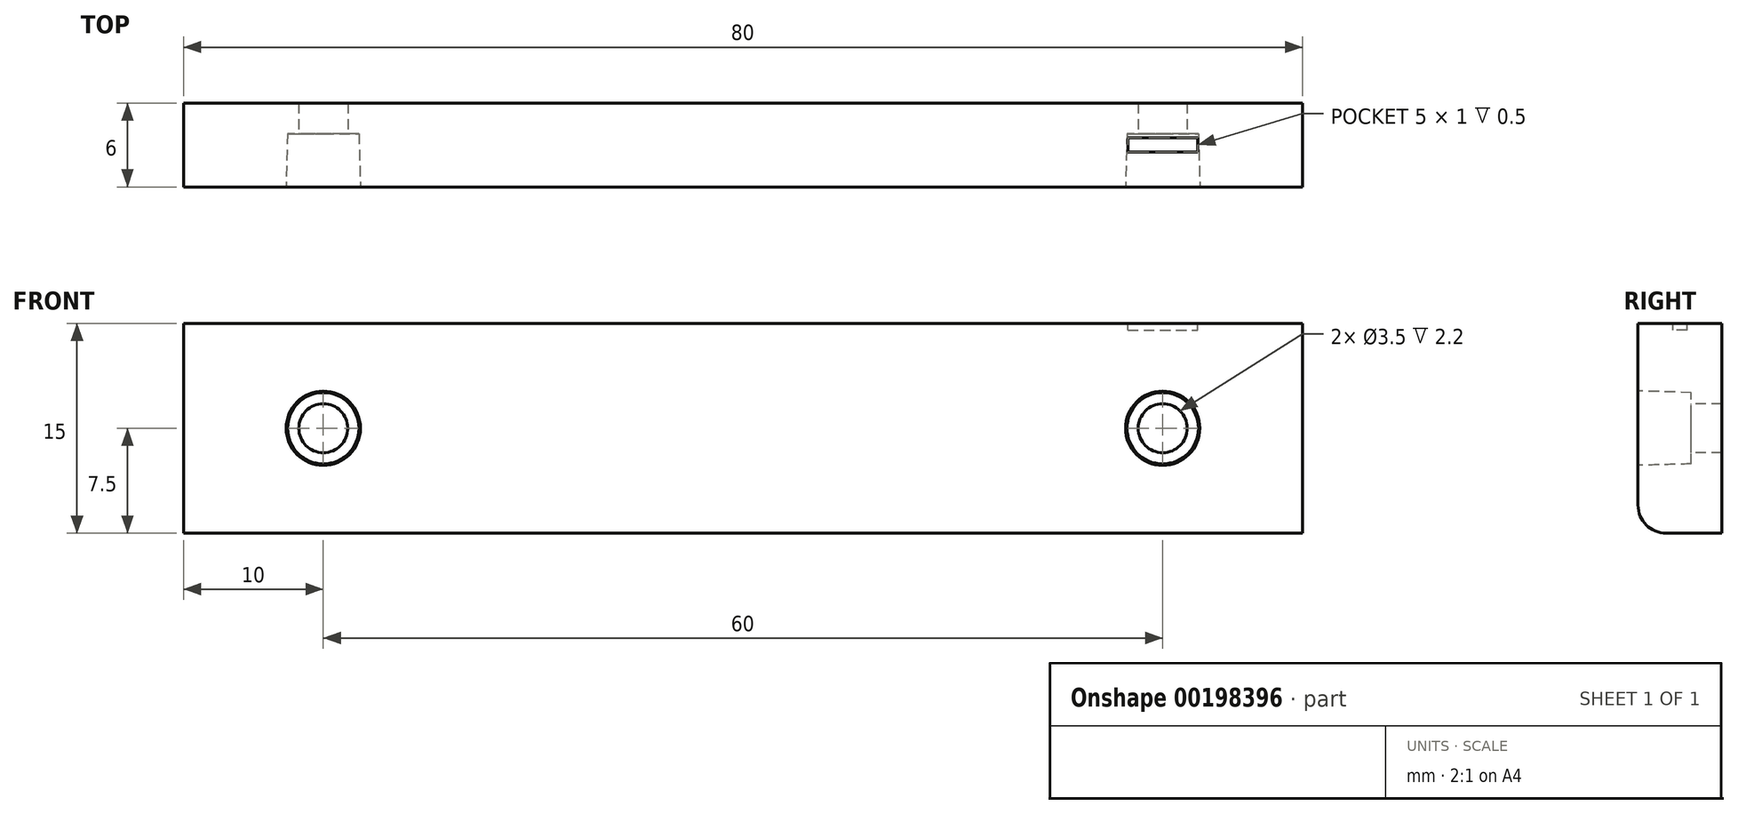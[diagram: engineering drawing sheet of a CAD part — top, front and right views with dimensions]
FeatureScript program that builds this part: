
annotation { "Feature Type Name" : "Feature", "Feature Type Description" : "" }
export const myFeature = defineFeature(function(context is Context, id is Id, definition is map)
    precondition{}
    {
        {
            var Q0;
            Q0=qCreatedBy(makeId("Top.planeOp"),FACE);
            var sketch = newSketch(context, id + "F0", { "sketchPlane" : qUnion([Q0])});
            skLineSegment(sketch, "E0.bottom", {"start": v(40, -3) * mm, "end": v(-40, -3) * mm});
            skLineSegment(sketch, "E0.top", {"start": v(40, 3) * mm, "end": v(-40, 3) * mm});
            skLineSegment(sketch, "E0.left", {"start": v(40, -3) * mm, "end": v(40, 3) * mm});
            skLineSegment(sketch, "E0.right", {"start": v(-40, -3) * mm, "end": v(-40, 3) * mm});
            skPoint(sketch, "E0.middle", {"position": v(0, 0) * mm});
            skSolve(sketch);
        }
        {
            var Q0;
            Q0=makeQuery(id+"F0.imprint","IMPRINT",FACE,{"disambiguationData":[TD([[makeQuery(id+"F0.imprint","IMPRINT",EDGE,{"derivedFrom":sQuery(id+"F0.wireOp",EDGE,"E0.bottom")}),-1.0]])]});
            extrude(context, id + "F1", {"entities" : qUnion([Q0]), "depth" : 15 * mm});
        }
        {
            var Q0;
            Q0=makeQuery(id+"F1.opExtrude","SWEPT_FACE",FACE,{"disambiguationData":[OSD([sQuery(id+"F0.wireOp",EDGE,"E0.bottom")])]});
            var sketch = newSketch(context, id + "F2", { "sketchPlane" : qUnion([Q0])});
            skPoint(sketch, "E1", {"position": v(-30, 7.5) * mm});
            skPoint(sketch, "E2", {"position": v(30, 7.5) * mm});
            skPoint(sketch, "E3", {"position": v(0, 7.5) * mm});
            skPoint(sketch, "E3.positionSnap0", {"position": v(0, 0) * mm});
            skCircle(sketch, "E4", {"center": v(-30, 7.5) * mm, "radius": 2.65 * mm});
            skCircle(sketch, "E5", {"center": v(30, 7.5) * mm, "radius": 2.65 * mm});
            skSolve(sketch);
        }
        {
            var Q0;
            Q0=makeQuery(id+"F2.imprint","IMPRINT",FACE,{"disambiguationData":[TD([[makeQuery(id+"F2.imprint","IMPRINT",EDGE,{"derivedFrom":sQuery(id+"F2.wireOp",EDGE,"E4")}),-1.0]])]});
            cPlane(context, id + "F3", {"entities" : qUnion([Q0]), "cplaneType" : CPlaneType.OFFSET, "offset" : 3.8 * mm, "oppositeDirection" : true, "width" : 150 * mm, "height" : 150 * mm});
        }
        {
            var Q0;
            Q0=qCreatedBy(id+"F3.planeOp",FACE);
            var sketch = newSketch(context, id + "F4", { "sketchPlane" : qUnion([Q0])});
            skCircle(sketch, "E6", {"center": v(-30, 7.5) * mm, "radius": 2.55 * mm});
            skCircle(sketch, "E7", {"center": v(30, 7.5) * mm, "radius": 2.55 * mm});
            skSolve(sketch);
        }
        {
            var Q1;
            Q1=makeQuery(id+"F4.imprint","IMPRINT",FACE,{"disambiguationData":[TD([[makeQuery(id+"F4.imprint","IMPRINT",EDGE,{"derivedFrom":sQuery(id+"F4.wireOp",EDGE,"E6")}),1.0]])]});
            var Q2;
            Q2=makeQuery(id+"F2.imprint","IMPRINT",FACE,{"disambiguationData":[TD([[makeQuery(id+"F2.imprint","IMPRINT",EDGE,{"derivedFrom":sQuery(id+"F2.wireOp",EDGE,"E4")}),1.0]])]});
            var Q3;
            Q3=sQuery(id+"F4.wireOp",EDGE,"E6");
            var Q4;
            Q4=sQuery(id+"F2.wireOp",EDGE,"E4");
            loft(context, id + "F5", {"operationType" : NewBodyOperationType.REMOVE, "sheetProfilesArray" : [{ "sheetProfileEntities" : qUnion([Q1]) }, { "sheetProfileEntities" : qUnion([Q2]) }], "wireProfilesArray" : [{ "wireProfileEntities" : qUnion([Q3]) }, { "wireProfileEntities" : qUnion([Q4]) }]});
        }
        {
            var Q1;
            Q1=makeQuery(id+"F2.imprint","IMPRINT",FACE,{"disambiguationData":[TD([[makeQuery(id+"F2.imprint","IMPRINT",EDGE,{"derivedFrom":sQuery(id+"F2.wireOp",EDGE,"E5")}),1.0]])]});
            var Q2;
            Q2=makeQuery(id+"F4.imprint","IMPRINT",FACE,{"disambiguationData":[TD([[makeQuery(id+"F4.imprint","IMPRINT",EDGE,{"derivedFrom":sQuery(id+"F4.wireOp",EDGE,"E7")}),1.0]])]});
            loft(context, id + "F6", {"operationType" : NewBodyOperationType.REMOVE, "sheetProfilesArray" : [{ "sheetProfileEntities" : qUnion([Q1]) }, { "sheetProfileEntities" : qUnion([Q2]) }]});
        }
        {
            var Q0;
            Q0=sQuery(id+"F4.wireOp",VERTEX,"E7.center");
            var Q1;
            Q1=sQuery(id+"F4.wireOp",VERTEX,"E6.center");
            var Q2;
            Q2=makeQuery(id+"F1.opExtrude","SWEPT_BODY",BODY,{"disambiguationData":[OSD([sQuery(id+"F0.wireOp",EDGE,"E0.bottom"),sQuery(id+"F0.wireOp",EDGE,"E0.top"),sQuery(id+"F0.wireOp",EDGE,"E0.left"),sQuery(id+"F0.wireOp",EDGE,"E0.right")])]});
            hole(context, id + "F7", {"style" : HoleStyle.SIMPLE, "endStyle" : HoleEndStyle.THROUGH, "holeDiameter" : 3.5 * mm, "startFromSketch" : true, "locations" : qUnion([Q0, Q1]), "scope" : qUnion([Q2]), "isTappedThrough" : true});
        }
        {
            var Q0;
            Q0=makeQuery(id+"F1.opExtrude","CAP_EDGE",EDGE,{"disambiguationData":[OSD([sQuery(id+"F0.wireOp",EDGE,"E0.bottom")])],"isStart":true});
            fillet(context, id + "F8", {"entities" : qUnion([Q0]), "radius" : 2 * mm, "tangentPropagation" : true, "allowEdgeOverflow" : false});
        }
        {
            var Q0;
            Q0=makeQuery(id+"F1.opExtrude","CAP_FACE",FACE,{"disambiguationData":[OSD([sQuery(id+"F0.wireOp",EDGE,"E0.bottom"),sQuery(id+"F0.wireOp",EDGE,"E0.top"),sQuery(id+"F0.wireOp",EDGE,"E0.left"),sQuery(id+"F0.wireOp",EDGE,"E0.right")])],"isStart":false});
            var sketch = newSketch(context, id + "F9", { "sketchPlane" : qUnion([Q0])});
            skLineSegment(sketch, "E8", {"start": v(-1.38, 0) * mm, "end": v(42.12, 0) * mm, "construction": true});
            skPoint(sketch, "E9.0", {"position": v(30, 0.8) * mm});
            skLineSegment(sketch, "E10", {"start": v(30, -3.6) * mm, "end": v(30, 4.08) * mm, "construction": true});
            skPoint(sketch, "E11", {"position": v(30, 0) * mm});
            skLineSegment(sketch, "E12.bottom", {"start": v(27.5, 0.5) * mm, "end": v(32.5, 0.5) * mm});
            skLineSegment(sketch, "E12.top", {"start": v(27.5, -0.5) * mm, "end": v(32.5, -0.5) * mm});
            skLineSegment(sketch, "E12.left", {"start": v(27.5, 0.5) * mm, "end": v(27.5, -0.5) * mm});
            skLineSegment(sketch, "E12.right", {"start": v(32.5, 0.5) * mm, "end": v(32.5, -0.5) * mm});
            skSolve(sketch);
        }
        {
            var Q0;
            Q0=makeQuery(id+"F9.imprint","IMPRINT",FACE,{"disambiguationData":[TD([[makeQuery(id+"F9.imprint","IMPRINT",EDGE,{"derivedFrom":sQuery(id+"F9.wireOp",EDGE,"E12.bottom")}),-1.0]])]});
            extrude(context, id + "F10", {"entities" : qUnion([Q0]), "operationType" : NewBodyOperationType.REMOVE, "oppositeDirection" : true, "depth" : .5 * mm});
        }
    });
